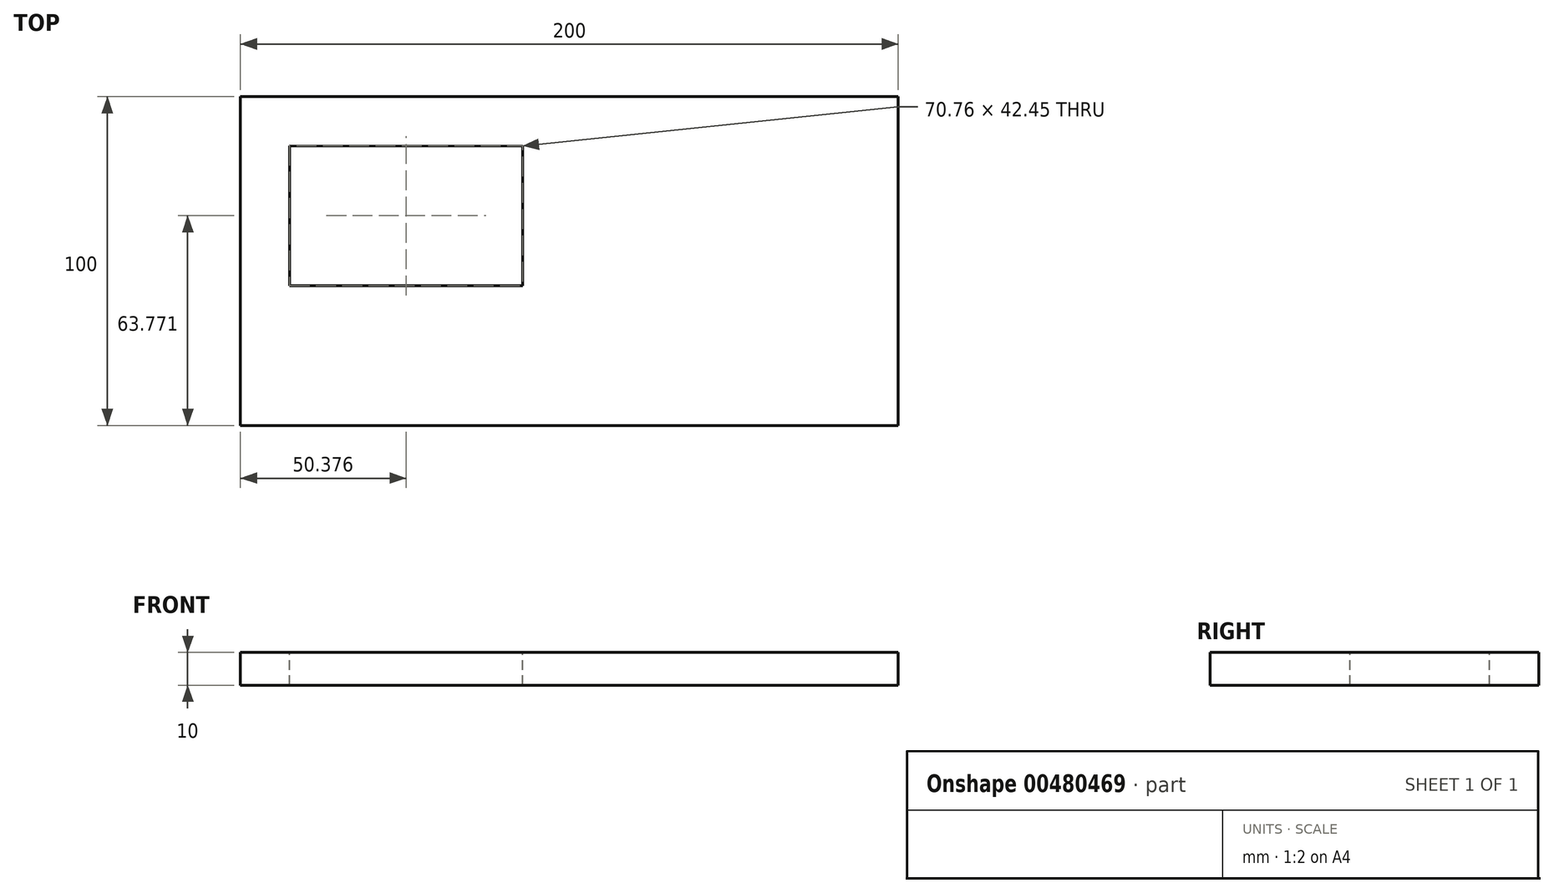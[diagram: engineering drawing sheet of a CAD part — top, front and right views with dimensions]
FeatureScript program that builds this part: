
annotation { "Feature Type Name" : "Feature", "Feature Type Description" : "" }
export const myFeature = defineFeature(function(context is Context, id is Id, definition is map)
    precondition{}
    {
        {
            var Q0;
            Q0=qCreatedBy(makeId("Top.planeOp"),FACE);
            var sketch = newSketch(context, id + "F0", { "sketchPlane" : qUnion([Q0])});
            skLineSegment(sketch, "E0.bottom", {"start": v(-91.06, 15.07) * mm, "end": v(108.94, 15.07) * mm});
            skLineSegment(sketch, "E0.top", {"start": v(-91.06, -84.93) * mm, "end": v(108.94, -84.93) * mm});
            skLineSegment(sketch, "E0.left", {"start": v(-91.06, 15.07) * mm, "end": v(-91.06, -84.93) * mm});
            skLineSegment(sketch, "E0.right", {"start": v(108.94, 15.07) * mm, "end": v(108.94, -84.93) * mm});
            skSolve(sketch);
        }
        {
            var Q0;
            Q0 = qSketchRegion(id + "F0", true);
            extrude(context, id + "F1", {"entities" : qUnion([Q0]), "depth" : 10 * mm});
        }
        {
            var Q0;
            Q0=makeQuery(id+"F1.opExtrude","CAP_FACE",FACE,{"disambiguationData":[OSD([sQuery(id+"F0.wireOp",EDGE,"E0.bottom"),sQuery(id+"F0.wireOp",EDGE,"E0.top"),sQuery(id+"F0.wireOp",EDGE,"E0.left"),sQuery(id+"F0.wireOp",EDGE,"E0.right")])],"isStart":false});
            var sketch = newSketch(context, id + "F2", { "sketchPlane" : qUnion([Q0])});
            skLineSegment(sketch, "E1", {"start": v(-5.3, 0) * mm, "end": v(-5.3, -42.39) * mm});
            skLineSegment(sketch, "E2", {"start": v(-5.3, -42.39) * mm, "end": v(-76.06, -42.39) * mm});
            skPoint(sketch, "E3.end.orphan", {"position": v(-76.06, -27.14) * mm});
            skLineSegment(sketch, "E4", {"start": v(-76.06, 0.07) * mm, "end": v(-76.06, -42.39) * mm});
            skLineSegment(sketch, "E5", {"start": v(-76.06, 0.07) * mm, "end": v(-5.3, 0) * mm});
            skSolve(sketch);
        }
        {
            var Q0;
            Q0 = qSketchRegion(id + "F2", true);
            extrude(context, id + "F3", {"entities" : qUnion([Q0]), "operationType" : NewBodyOperationType.REMOVE, "oppositeDirection" : true, "depth" : 25 * mm});
        }
    });
